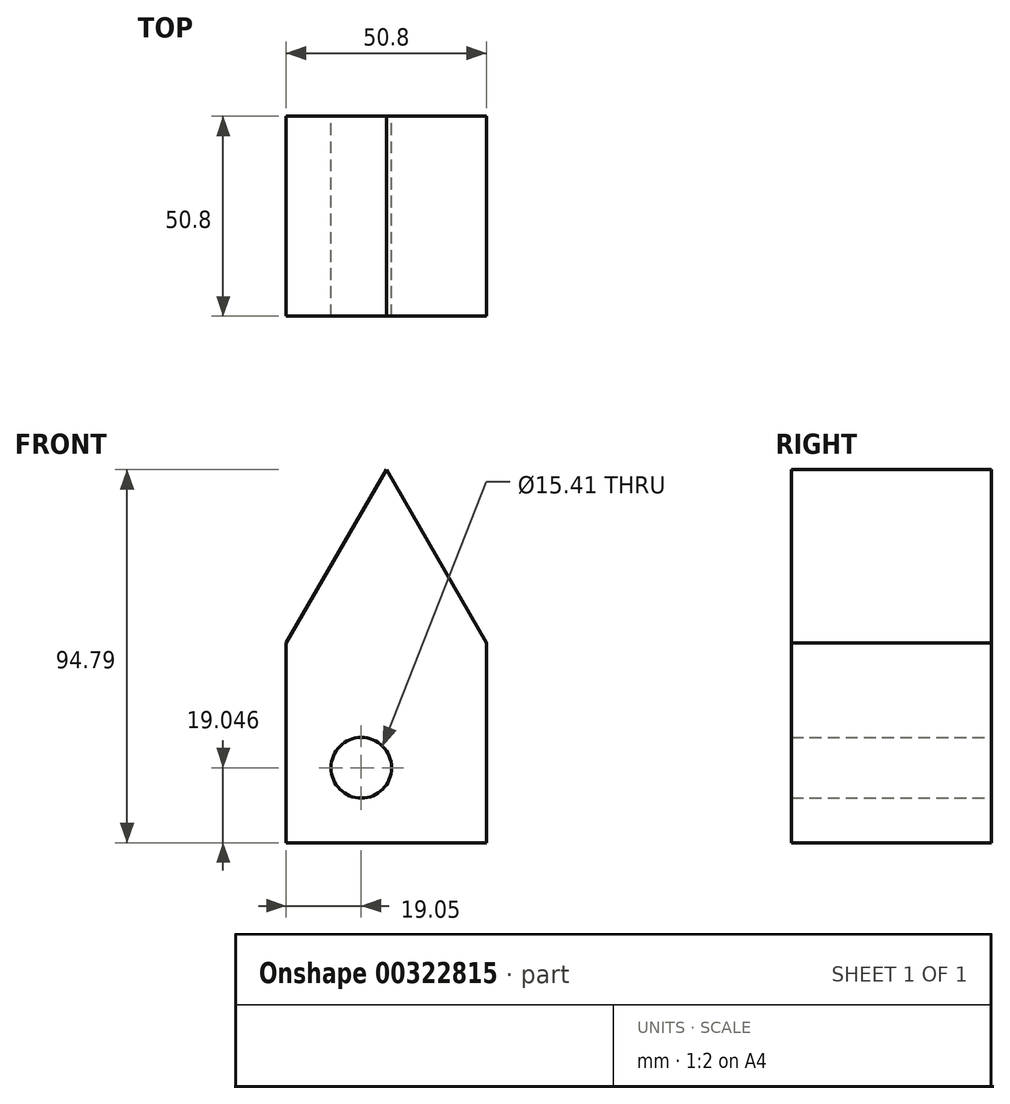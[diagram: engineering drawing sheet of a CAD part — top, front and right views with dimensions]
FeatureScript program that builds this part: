
annotation { "Feature Type Name" : "Feature", "Feature Type Description" : "" }
export const myFeature = defineFeature(function(context is Context, id is Id, definition is map)
    precondition{}
    {
        {
            var Q0;
            Q0=qCreatedBy(makeId("Front.planeOp"),FACE);
            var sketch = newSketch(context, id + "F0", { "sketchPlane" : qUnion([Q0])});
            skLineSegment(sketch, "E0.top", {"start": v(-25.4, -28.56) * mm, "end": v(25.4, -28.56) * mm});
            skLineSegment(sketch, "E0.left", {"start": v(-25.4, 22.24) * mm, "end": v(-25.4, -28.56) * mm});
            skLineSegment(sketch, "E0.right", {"start": v(25.4, 22.24) * mm, "end": v(25.4, -28.56) * mm});
            skLineSegment(sketch, "E1", {"start": v(25.4, 22.24) * mm, "end": v(0, 66.23) * mm});
            skLineSegment(sketch, "E2", {"start": v(-25.4, 22.24) * mm, "end": v(0, 66.23) * mm});
            skCircle(sketch, "E3", {"center": v(-6.35, -9.51) * mm, "radius": 7.7 * mm});
            skSolve(sketch);
        }
        {
            var Q0;
            Q0=makeQuery(id+"F0.imprint","IMPRINT",FACE,{"disambiguationData":[TD([[makeQuery(id+"F0.imprint","IMPRINT",EDGE,{"derivedFrom":sQuery(id+"F0.wireOp",EDGE,"E0.top")}),1.0]])]});
            extrude(context, id + "F1", {"entities" : qUnion([Q0]), "depth" : 50.8 * mm});
        }
    });
